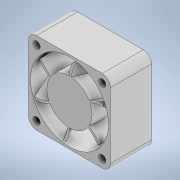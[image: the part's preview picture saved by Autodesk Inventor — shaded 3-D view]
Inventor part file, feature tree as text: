
AUTODESK INVENTOR PART (.ipt)
format: ipt  version: 2022 (Build 260153070, 153G)  size: 289,280 bytes
history: native  units: in
note: dims shown in document units (in); Inventor stores cm internally (conversion verified against a paired STEP export)
features: sketch x5, extrude x3, fillet x1, plane x1, loft x1, pattern_circular x1
ambient origin geometry x8: Origin, YZ Plane, XZ Plane, XY Plane, X Axis, Y Axis, Z Axis, Center Point
bodies: Solid1 (feature_tree)
feature tree (12):
  extrude  "Extrusion1"  Depth=1.2598in
  extrude  "Extrusion2"  Depth=0.1378in
  fillet  "Fillet1"  Radius=0.1378in
  sketch  "Sketch3"  dims[d7=0.1378in d8=1.4961in d9=0.7874in d10=0.0in]
  plane  "Work Plane1"
  loft  "Loft2"
  pattern_circular  "Circular Pattern1"  Count=2  [1 undecoded]
  extrude  "Extrusion3"  Depth=0.7087in TaperAngle=0.0deg
  sketch  "Sketch1"  dims[d0=1.5748in d3=1.2598in]
  sketch  "Sketch2"  dims[d4=0.1378in d5=0.1378in d6=0.1378in]
  sketch  "Sketch4"  dims[d11=0.8661in d12=0.7087in d13=0.0in]
  sketch  "Sketch5"  dims[d14=0.0787in d15=1.4961in d17=0.0344in d19=0.055in d20=-0.6299in d21=0.0344in d23=0.055in d24=30.0deg d29=0.0in d30=90.0deg d31=0.0in d32=90.0deg d33=2.3622in d34=360.0deg d36=0.0394in d37=0.7087in d38=0.0in]
note: 1 required parameter value undecoded (feature->parameter linkage not recoverable at this tier; creation-order binding heuristic only, values carry confidence <= 0.55)
